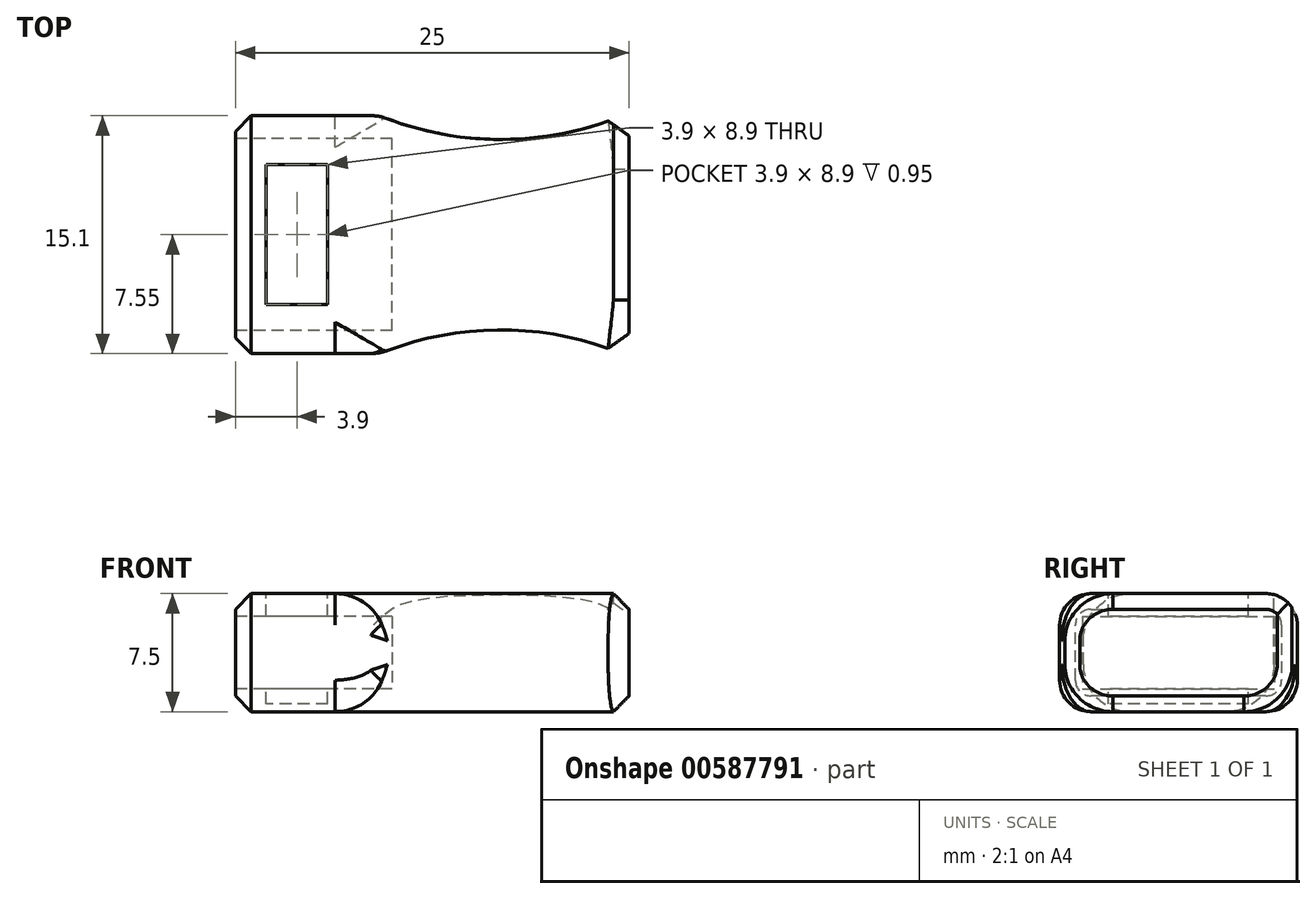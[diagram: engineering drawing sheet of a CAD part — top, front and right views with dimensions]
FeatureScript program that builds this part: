
annotation { "Feature Type Name" : "Feature", "Feature Type Description" : "" }
export const myFeature = defineFeature(function(context is Context, id is Id, definition is map)
    precondition{}
    {
        {
            var Q0;
            Q0=qCreatedBy(makeId("Top.planeOp"),FACE);
            var sketch = newSketch(context, id + "F0", { "sketchPlane" : qUnion([Q0])});
            skLineSegment(sketch, "E0.bottom", {"start": v(25, 7.55) * mm, "end": v(0, 7.55) * mm});
            skLineSegment(sketch, "E0.top", {"start": v(25, -7.55) * mm, "end": v(0, -7.55) * mm});
            skLineSegment(sketch, "E0.left", {"start": v(25, 7.55) * mm, "end": v(25, -7.55) * mm});
            skLineSegment(sketch, "E0.right", {"start": v(0, 7.55) * mm, "end": v(0, -7.55) * mm});
            skPoint(sketch, "E0.middle", {"position": v(0, 0) * mm});
            skSolve(sketch);
        }
        {
            var Q0;
            Q0=qSketchRegion(id+"F0",true);
            extrude(context, id + "F1", {"entities" : qUnion([Q0]), "depth" : 7.5 * mm, "offsetDistance" : 25 * mm});
        }
        {
            var Q0;
            Q0=makeQuery(id+"F1.opExtrude","SWEPT_FACE",FACE,{"disambiguationData":[OSD([sQuery(id+"F0.wireOp",EDGE,"E0.right")])]});
            var sketch = newSketch(context, id + "F2", { "sketchPlane" : qUnion([Q0])});
            skLineSegment(sketch, "E1.bottom", {"start": v(6.1, 6.05) * mm, "end": v(-6.1, 6.05) * mm});
            skLineSegment(sketch, "E1.top", {"start": v(6.1, 1.45) * mm, "end": v(-6.1, 1.45) * mm});
            skLineSegment(sketch, "E1.left", {"start": v(6.1, 6.05) * mm, "end": v(6.1, 1.45) * mm});
            skLineSegment(sketch, "E1.right", {"start": v(-6.1, 6.05) * mm, "end": v(-6.1, 1.45) * mm});
            skPoint(sketch, "E1.middle", {"position": v(0, 3.75) * mm});
            skSolve(sketch);
        }
        {
            var Q0;
            Q0=qSketchRegion(id+"F2",true);
            extrude(context, id + "F3", {"entities" : qUnion([Q0]), "operationType" : NewBodyOperationType.REMOVE, "oppositeDirection" : true, "depth" : 9.95 * mm, "offsetDistance" : 25 * mm});
        }
        {
            var Q0;
            Q0=makeQuery(id+"F1.opExtrude","CAP_FACE",FACE,{"disambiguationData":[OSD([sQuery(id+"F0.wireOp",EDGE,"E0.bottom"),sQuery(id+"F0.wireOp",EDGE,"E0.top"),sQuery(id+"F0.wireOp",EDGE,"E0.left"),sQuery(id+"F0.wireOp",EDGE,"E0.right")])],"isStart":false});
            var sketch = newSketch(context, id + "F4", { "sketchPlane" : qUnion([Q0])});
            skLineSegment(sketch, "E2.bottom", {"start": v(5.85, 4.45) * mm, "end": v(1.95, 4.45) * mm});
            skLineSegment(sketch, "E2.top", {"start": v(5.85, -4.45) * mm, "end": v(1.95, -4.45) * mm});
            skLineSegment(sketch, "E2.left", {"start": v(5.85, 4.45) * mm, "end": v(5.85, -4.45) * mm});
            skLineSegment(sketch, "E2.right", {"start": v(1.95, 4.45) * mm, "end": v(1.95, -4.45) * mm});
            skPoint(sketch, "E2.middle", {"position": v(3.9, 0) * mm});
            skSolve(sketch);
        }
        {
            var Q0;
            Q0=qSketchRegion(id+"F4",true);
            extrude(context, id + "F5", {"entities" : qUnion([Q0]), "operationType" : NewBodyOperationType.REMOVE, "oppositeDirection" : true, "depth" : 25 * mm, "offsetDistance" : 25 * mm});
        }
        {
            var Q0;
            Q0=makeQuery(id+"F1.opExtrude","CAP_FACE",FACE,{"disambiguationData":[OSD([sQuery(id+"F0.wireOp",EDGE,"E0.bottom"),sQuery(id+"F0.wireOp",EDGE,"E0.top"),sQuery(id+"F0.wireOp",EDGE,"E0.left"),sQuery(id+"F0.wireOp",EDGE,"E0.right")])],"isStart":false});
            var sketch = newSketch(context, id + "F6", { "sketchPlane" : qUnion([Q0])});
            skCircle(sketch, "E3", {"center": v(16.85, 26.55) * mm, "radius": 20.5 * mm});
            skCircle(sketch, "E4", {"center": v(16.85, -26.55) * mm, "radius": 20.5 * mm});
            skSolve(sketch);
        }
        {
            var Q0;
            Q0=qSketchRegion(id+"F6",true);
            extrude(context, id + "F7", {"entities" : qUnion([Q0]), "operationType" : NewBodyOperationType.REMOVE, "oppositeDirection" : true, "depth" : 25 * mm, "offsetDistance" : 25 * mm});
        }
        {
            var Q0;
            Q0=makeQuery(id+"F1.opExtrude","CAP_FACE",FACE,{"disambiguationData":[OSD([sQuery(id+"F0.wireOp",EDGE,"E0.bottom"),sQuery(id+"F0.wireOp",EDGE,"E0.top"),sQuery(id+"F0.wireOp",EDGE,"E0.left"),sQuery(id+"F0.wireOp",EDGE,"E0.right")])],"isStart":true});
            var sketch = newSketch(context, id + "F8", { "sketchPlane" : qUnion([Q0])});
            skLineSegment(sketch, "E5.bottom", {"start": v(1.46, 4.94) * mm, "end": v(8.37, 4.94) * mm});
            skLineSegment(sketch, "E5.top", {"start": v(1.46, -5) * mm, "end": v(8.37, -5) * mm});
            skLineSegment(sketch, "E5.left", {"start": v(1.46, 4.94) * mm, "end": v(1.46, -5) * mm});
            skLineSegment(sketch, "E5.right", {"start": v(8.37, 4.94) * mm, "end": v(8.37, -5) * mm});
            skSolve(sketch);
        }
        {
            var Q0;
            Q0=qSketchRegion(id+"F8",true);
            extrude(context, id + "F9", {"entities" : qUnion([Q0]), "operationType" : NewBodyOperationType.ADD, "oppositeDirection" : true, "depth" : .5 * mm, "offsetDistance" : 25 * mm});
        }
        {
            var Q0;
            Q0=makeQuery(id+"F7.boolean.opBoolean","COPY",EDGE,{"derivedFrom":makeQuery(id+"F7.opExtrude","CAP_EDGE",EDGE,{"disambiguationData":[OSD([sQuery(id+"F6.wireOp",EDGE,"E4")])],"isStart":true})});
            var Q1;
            Q1=makeQuery(id+"F7.boolean.opBoolean","COPY",FACE,{"derivedFrom":makeQuery(id+"F7.opExtrude","SWEPT_FACE",FACE,{"disambiguationData":[OSD([sQuery(id+"F6.wireOp",EDGE,"E4")])]})});
            var Q2;
            Q2=makeQuery(id+"F7.boolean.opBoolean","COPY",EDGE,{"derivedFrom":makeQuery(id+"F7.opExtrude","CAP_EDGE",EDGE,{"disambiguationData":[OSD([sQuery(id+"F6.wireOp",EDGE,"E3")])],"isStart":true})});
            var Q3;
            Q3=makeQuery(id+"F7.boolean.opBoolean","INTERSECT",EDGE,{"derivedFrom":[makeQuery(id+"F1.opExtrude","CAP_FACE",FACE,{"disambiguationData":[OSD([sQuery(id+"F0.wireOp",EDGE,"E0.bottom"),sQuery(id+"F0.wireOp",EDGE,"E0.top"),sQuery(id+"F0.wireOp",EDGE,"E0.left"),sQuery(id+"F0.wireOp",EDGE,"E0.right")])],"isStart":true}),makeQuery(id+"F7.opExtrude","SWEPT_FACE",FACE,{"disambiguationData":[OSD([sQuery(id+"F6.wireOp",EDGE,"E3")])]})]});
            fillet(context, id + "F10", {"entities" : qUnion([Q0, Q1, Q2, Q3]), "radius" : 3 * mm, "tangentPropagation" : true, "allowEdgeOverflow" : false});
        }
        {
            var Q0;
            {var subQ0=sQuery(id+"F0.wireOp",EDGE,"E0.bottom");var subQ1=sQuery(id+"F0.wireOp",EDGE,"E0.right");Q0=makeQuery(id+"F7.boolean.opBoolean","SPLIT",EDGE,{"disambiguationData":[TD([makeQuery(id+"F1.opExtrude","SWEPT_FACE",FACE,{"disambiguationData":[OSD([subQ1])]})])],"derivedFrom":makeQuery(id+"F1.opExtrude","CAP_EDGE",EDGE,{"disambiguationData":[OSD([subQ0])],"isStart":false})});}
            var Q1;
            {var subQ0=sQuery(id+"F0.wireOp",EDGE,"E0.right");var subQ1=sQuery(id+"F0.wireOp",EDGE,"E0.top");Q1=makeQuery(id+"F7.boolean.opBoolean","SPLIT",EDGE,{"disambiguationData":[TD([makeQuery(id+"F1.opExtrude","SWEPT_FACE",FACE,{"disambiguationData":[OSD([subQ0])]})])],"derivedFrom":makeQuery(id+"F1.opExtrude","CAP_EDGE",EDGE,{"disambiguationData":[OSD([subQ1])],"isStart":false})});}
            var Q2;
            {var subQ0=sQuery(id+"F0.wireOp",EDGE,"E0.bottom");var subQ1=sQuery(id+"F0.wireOp",EDGE,"E0.right");Q2=makeQuery(id+"F7.boolean.opBoolean","SPLIT",EDGE,{"disambiguationData":[TD([makeQuery(id+"F1.opExtrude","SWEPT_FACE",FACE,{"disambiguationData":[OSD([subQ1])]})])],"derivedFrom":makeQuery(id+"F1.opExtrude","CAP_EDGE",EDGE,{"disambiguationData":[OSD([subQ0])],"isStart":true})});}
            var Q3;
            {var subQ0=sQuery(id+"F0.wireOp",EDGE,"E0.right");var subQ1=sQuery(id+"F0.wireOp",EDGE,"E0.top");Q3=makeQuery(id+"F7.boolean.opBoolean","SPLIT",EDGE,{"disambiguationData":[TD([makeQuery(id+"F1.opExtrude","SWEPT_FACE",FACE,{"disambiguationData":[OSD([subQ0])]})])],"derivedFrom":makeQuery(id+"F1.opExtrude","CAP_EDGE",EDGE,{"disambiguationData":[OSD([subQ1])],"isStart":true})});}
            fillet(context, id + "F11", {"entities" : qUnion([Q0, Q1, Q2, Q3]), "radius" : 2 * mm, "tangentPropagation" : true, "allowEdgeOverflow" : false});
        }
        {
            var Q0;
            {var subQ0=sQuery(id+"F0.wireOp",EDGE,"E0.right");var subQ1=makeQuery(id+"F1.opExtrude","SWEPT_FACE",FACE,{"disambiguationData":[OSD([subQ0])]});var subQ2=sQuery(id+"F0.wireOp",EDGE,"E0.top");Q0=makeQuery(id+"F11.opFillet","BLEND_EDGE",EDGE,{"blendedFrom":[makeQuery(id+"F7.boolean.opBoolean","SPLIT",EDGE,{"disambiguationData":[TD([subQ1])],"derivedFrom":makeQuery(id+"F1.opExtrude","CAP_EDGE",EDGE,{"disambiguationData":[OSD([subQ2])],"isStart":true})}),subQ1],"blendedInto":[subQ1]});}
            var Q1;
            Q1=makeQuery(id+"F1.opExtrude","SWEPT_FACE",FACE,{"disambiguationData":[OSD([sQuery(id+"F0.wireOp",EDGE,"E0.left")])]});
            chamfer(context, id + "F12", {"entities" : qUnion([Q0, Q1]), "width" : 1 * mm, "tangentPropagation" : true});
        }
    });
